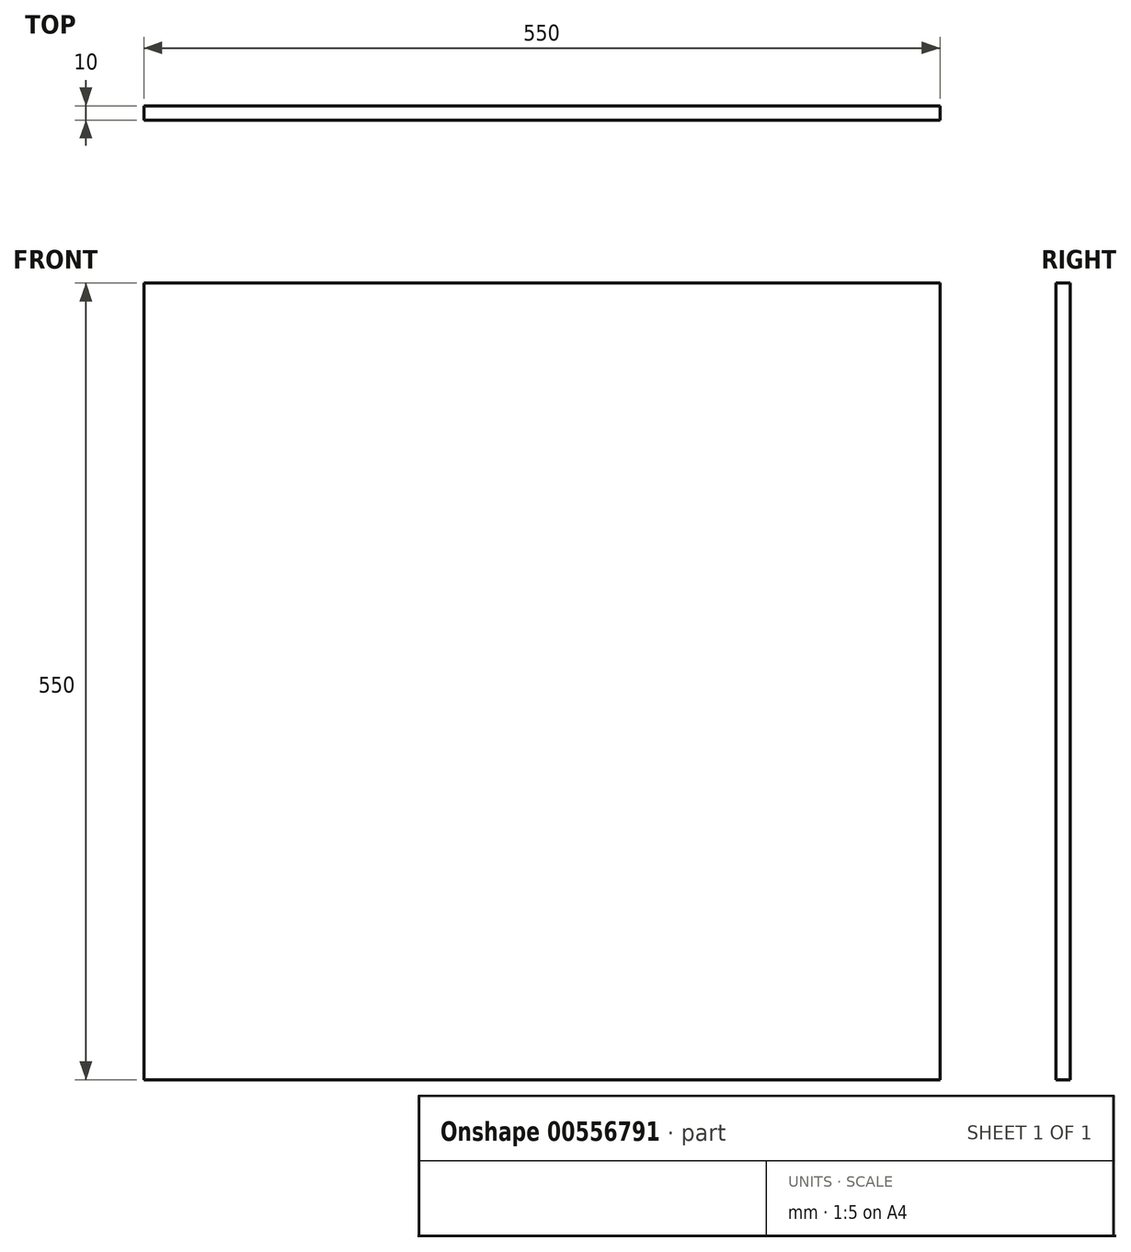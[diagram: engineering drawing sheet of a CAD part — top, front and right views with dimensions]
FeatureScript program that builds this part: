
annotation { "Feature Type Name" : "Feature", "Feature Type Description" : "" }
export const myFeature = defineFeature(function(context is Context, id is Id, definition is map)
    precondition{}
    {
        {
            var Q0;
            Q0=qCreatedBy(makeId("Front.planeOp"),FACE);
            var sketch = newSketch(context, id + "F0", { "sketchPlane" : qUnion([Q0])});
            skLineSegment(sketch, "E0.bottom", {"start": v(-275, 275) * mm, "end": v(275, 275) * mm});
            skLineSegment(sketch, "E0.top", {"start": v(-275, -275) * mm, "end": v(275, -275) * mm});
            skLineSegment(sketch, "E0.left", {"start": v(-275, 275) * mm, "end": v(-275, -275) * mm});
            skLineSegment(sketch, "E0.right", {"start": v(275, 275) * mm, "end": v(275, -275) * mm});
            skPoint(sketch, "E0.middle", {"position": v(0, 0) * mm});
            skSolve(sketch);
        }
        {
            var Q0;
            Q0=qSketchRegion(id+"F0",true);
            extrude(context, id + "F1", {"entities" : qUnion([Q0]), "depth" : 10 * mm, "offsetDistance" : 25 * mm});
        }
    });
